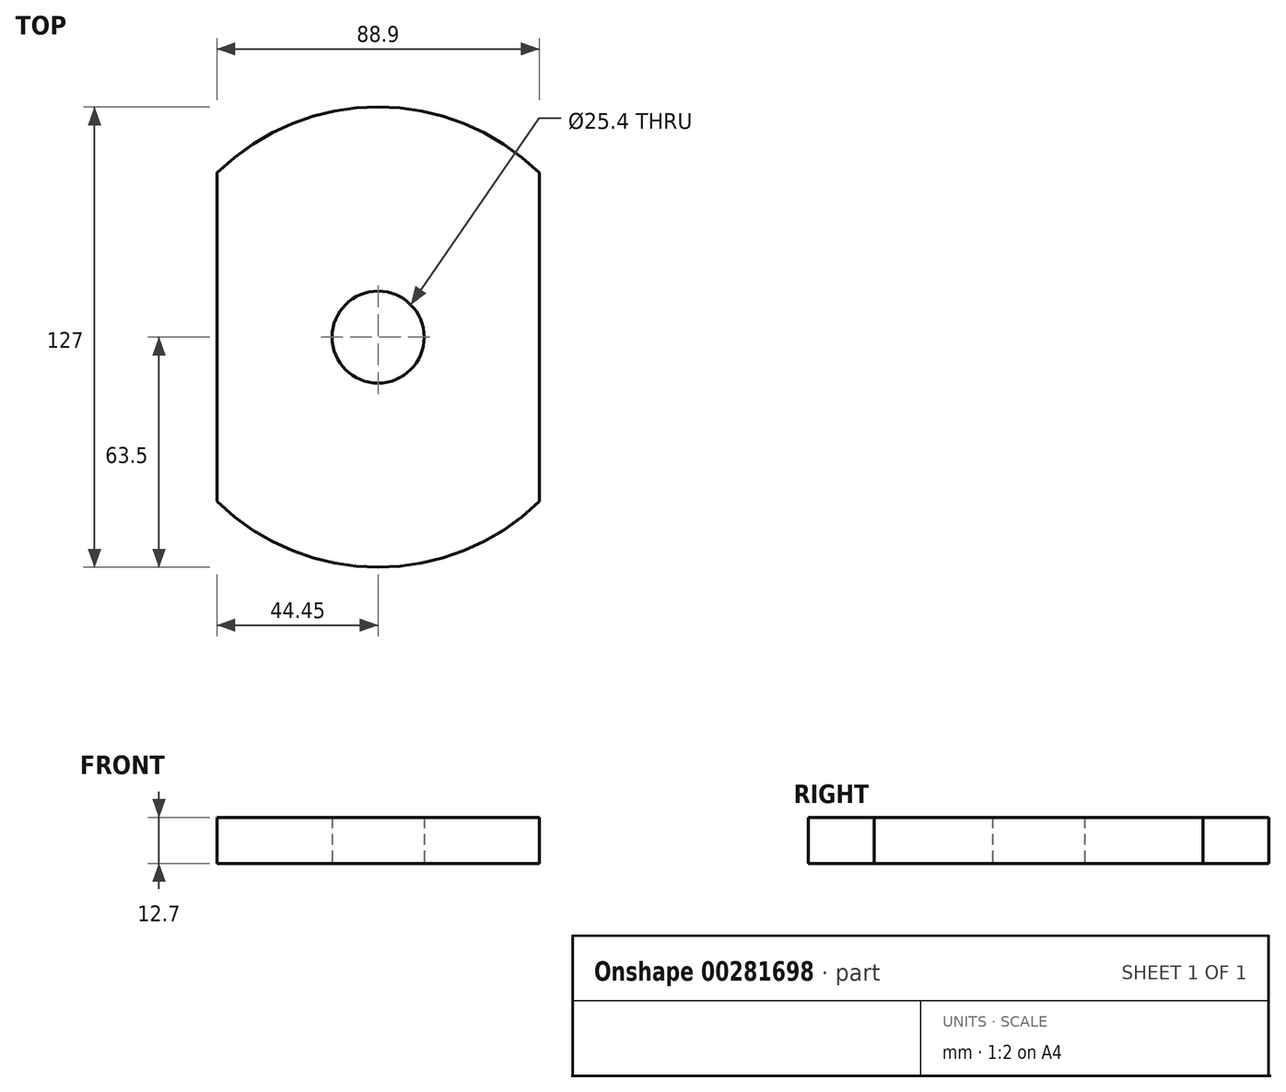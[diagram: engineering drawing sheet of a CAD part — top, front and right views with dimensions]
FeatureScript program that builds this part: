
annotation { "Feature Type Name" : "Feature", "Feature Type Description" : "" }
export const myFeature = defineFeature(function(context is Context, id is Id, definition is map)
    precondition{}
    {
        {
            var Q0;
            Q0=qCreatedBy(makeId("Top.planeOp"),FACE);
            var sketch = newSketch(context, id + "F0", { "sketchPlane" : qUnion([Q0])});
            skCircle(sketch, "E0", {"center": v(0, 0) * mm, "radius": 12.7 * mm});
            skCircle(sketch, "E1", {"center": v(0, 0) * mm, "radius": 63.5 * mm});
            skSolve(sketch);
        }
        {
            var Q0;
            Q0 = qSketchRegion(id + "F0", true);
            extrude(context, id + "F1", {"entities" : qUnion([Q0]), "depth" : 12.7 * mm});
        }
        {
            var Q0;
            Q0=makeQuery(id+"F1.opExtrude","CAP_FACE",FACE,{"disambiguationData":[OSD([sQuery(id+"F0.wireOp",EDGE,"E0"),sQuery(id+"F0.wireOp",EDGE,"E1")])],"isStart":false});
            var sketch = newSketch(context, id + "F2", { "sketchPlane" : qUnion([Q0])});
            skSolve(sketch);
        }
        {
            var Q0;
            Q0=makeQuery(id+"F2.imprint","IMPRINT",FACE,{"disambiguationData":[TD([[makeQuery(id+"F2.imprint","IMPRINT",EDGE,{"derivedFrom":makeQuery(id+"F1.opExtrude","CAP_EDGE",EDGE,{"disambiguationData":[OSD([sQuery(id+"F0.wireOp",EDGE,"E0")])],"isStart":false})}),-1.0]])]});
            var sketch = newSketch(context, id + "F3", { "sketchPlane" : qUnion([Q0])});
            skLineSegment(sketch, "E2.bottom", {"start": v(-98.48, 66.52) * mm, "end": v(-44.45, 66.52) * mm});
            skLineSegment(sketch, "E2.top", {"start": v(-98.48, -73.92) * mm, "end": v(-44.45, -73.92) * mm});
            skLineSegment(sketch, "E2.left", {"start": v(-98.48, 66.52) * mm, "end": v(-98.48, -73.92) * mm});
            skLineSegment(sketch, "E2.right", {"start": v(-44.45, 66.52) * mm, "end": v(-44.45, -73.92) * mm});
            skLineSegment(sketch, "E3.bottom", {"start": v(44.45, 67.1) * mm, "end": v(111.13, 67.1) * mm});
            skLineSegment(sketch, "E3.top", {"start": v(44.45, -73.92) * mm, "end": v(111.13, -73.92) * mm});
            skLineSegment(sketch, "E3.left", {"start": v(44.45, 67.1) * mm, "end": v(44.45, -73.92) * mm});
            skLineSegment(sketch, "E3.right", {"start": v(111.13, 67.1) * mm, "end": v(111.13, -73.92) * mm});
            skSolve(sketch);
        }
        {
            var Q0;
            Q0 = qSketchRegion(id + "F3", true);
            extrude(context, id + "F4", {"entities" : qUnion([Q0]), "operationType" : NewBodyOperationType.REMOVE, "oppositeDirection" : true, "depth" : 25.4 * mm});
        }
    });
